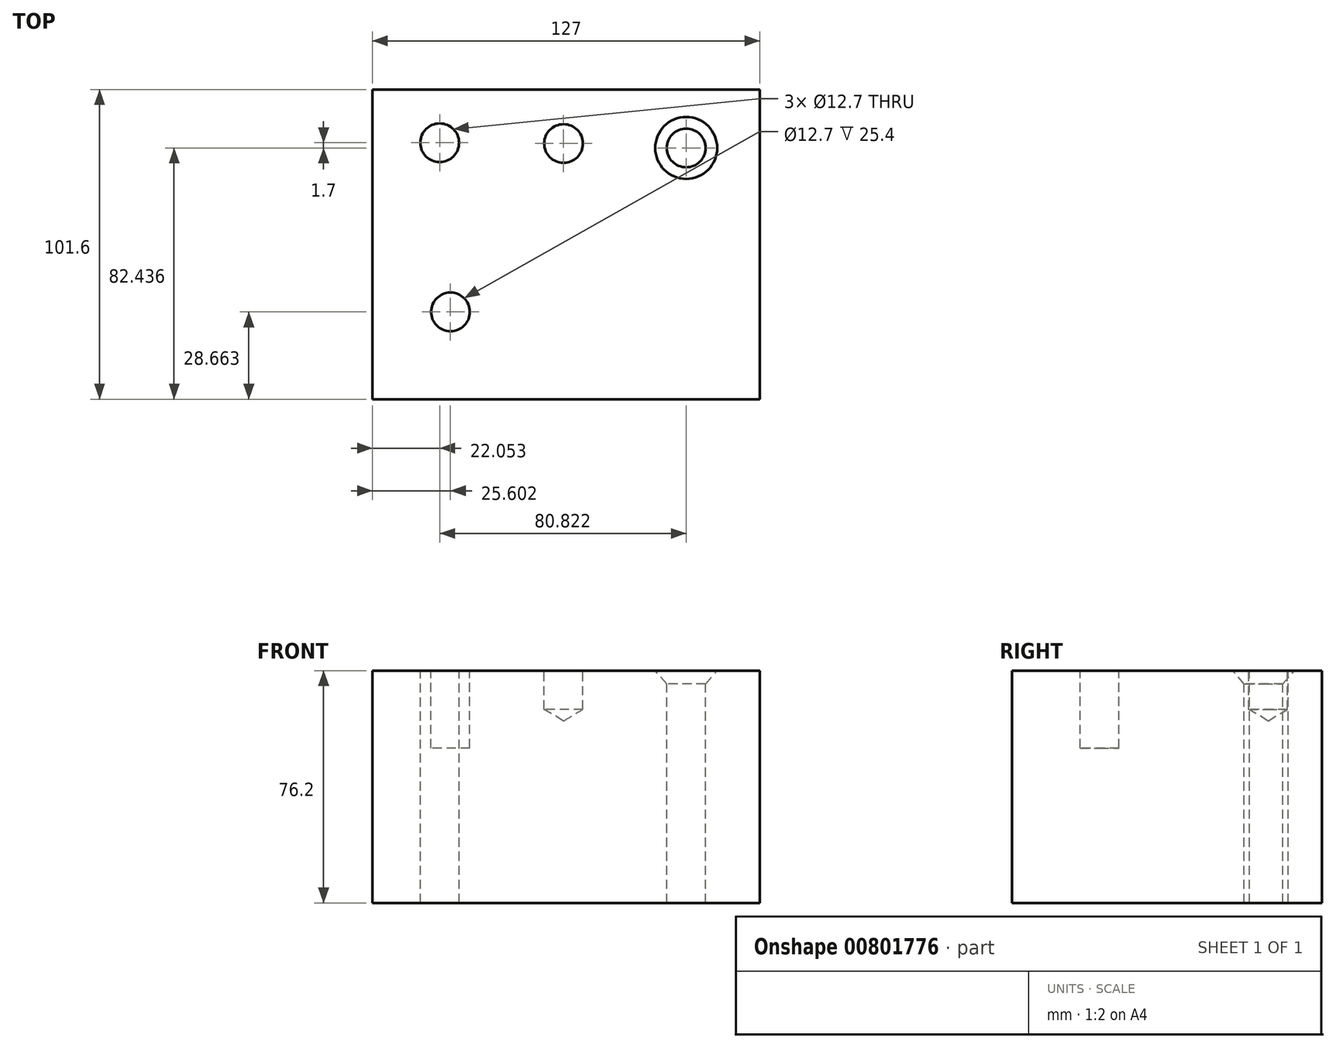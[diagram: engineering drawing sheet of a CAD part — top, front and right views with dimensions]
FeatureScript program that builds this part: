
annotation { "Feature Type Name" : "Feature", "Feature Type Description" : "" }
export const myFeature = defineFeature(function(context is Context, id is Id, definition is map)
    precondition{}
    {
        {
            var Q0;
            Q0=qCreatedBy(makeId("Top.planeOp"),FACE);
            var sketch = newSketch(context, id + "F0", { "sketchPlane" : qUnion([Q0])});
            skLineSegment(sketch, "E0.bottom", {"start": v(-55.05, 51.24) * mm, "end": v(71.95, 51.24) * mm});
            skLineSegment(sketch, "E0.top", {"start": v(-55.05, -50.36) * mm, "end": v(71.95, -50.36) * mm});
            skLineSegment(sketch, "E0.left", {"start": v(-55.05, 51.24) * mm, "end": v(-55.05, -50.36) * mm});
            skLineSegment(sketch, "E0.right", {"start": v(71.95, 51.24) * mm, "end": v(71.95, -50.36) * mm});
            skSolve(sketch);
        }
        {
            var Q0;
            Q0 = qSketchRegion(id + "F0", true);
            extrude(context, id + "F1", {"entities" : qUnion([Q0]), "depth" : 76.2 * mm, "offsetDistance" : 25.4 * mm});
        }
        {
            var Q0;
            Q0=makeQuery(id+"F1.opExtrude","CAP_FACE",FACE,{"disambiguationData":[OSD([sQuery(id+"F0.wireOp",EDGE,"E0.bottom"),sQuery(id+"F0.wireOp",EDGE,"E0.top"),sQuery(id+"F0.wireOp",EDGE,"E0.left"),sQuery(id+"F0.wireOp",EDGE,"E0.right")])],"isStart":false});
            var sketch = newSketch(context, id + "F2", { "sketchPlane" : qUnion([Q0])});
            skPoint(sketch, "E1", {"position": v(-33, 33.78) * mm});
            skPoint(sketch, "E2", {"position": v(7.63, 33.53) * mm});
            skPoint(sketch, "E3", {"position": v(47.83, 32.08) * mm});
            skPoint(sketch, "E4", {"position": v(-14.33, -25.97) * mm});
            skPoint(sketch, "E5", {"position": v(32.2, -27.84) * mm});
            skPoint(sketch, "E6", {"position": v(3.23, 2.39) * mm});
            skSolve(sketch);
        }
        {
            var Q0;
            Q0=sQuery(id+"F2.wireOp",VERTEX,"E1");
            var Q1;
            Q1=makeQuery(id+"F1.opExtrude","SWEPT_BODY",BODY,{"disambiguationData":[OSD([sQuery(id+"F0.wireOp",EDGE,"E0.bottom"),sQuery(id+"F0.wireOp",EDGE,"E0.top"),sQuery(id+"F0.wireOp",EDGE,"E0.left"),sQuery(id+"F0.wireOp",EDGE,"E0.right")])]});
            hole(context, id + "F3", {"style" : HoleStyle.SIMPLE, "endStyle" : HoleEndStyle.THROUGH, "holeDiameter" : 12.7 * mm, "majorDiameter" : 6.35 * mm, "isTappedThrough" : true, "tappedDepth" : 12.7 * mm, "tapClearance" : 3, "locations" : qUnion([Q0]), "scope" : qUnion([Q1])});
        }
        {
            var Q0;
            Q0=sQuery(id+"F2.wireOp",VERTEX,"E2");
            var Q1;
            Q1=makeQuery(id+"F1.opExtrude","SWEPT_BODY",BODY,{"disambiguationData":[OSD([sQuery(id+"F0.wireOp",EDGE,"E0.bottom"),sQuery(id+"F0.wireOp",EDGE,"E0.top"),sQuery(id+"F0.wireOp",EDGE,"E0.left"),sQuery(id+"F0.wireOp",EDGE,"E0.right")])]});
            hole(context, id + "F4", {"style" : HoleStyle.SIMPLE, "endStyle" : HoleEndStyle.BLIND, "holeDiameter" : 12.7 * mm, "majorDiameter" : 6.35 * mm, "holeDepth" : 12.7 * mm, "isTappedThrough" : true, "tappedDepth" : 12.7 * mm, "tapClearance" : 3, "locations" : qUnion([Q0]), "scope" : qUnion([Q1])});
        }
        {
            var Q0;
            Q0=sQuery(id+"F2.wireOp",VERTEX,"E3");
            var Q1;
            Q1=makeQuery(id+"F1.opExtrude","SWEPT_BODY",BODY,{"disambiguationData":[OSD([sQuery(id+"F0.wireOp",EDGE,"E0.bottom"),sQuery(id+"F0.wireOp",EDGE,"E0.top"),sQuery(id+"F0.wireOp",EDGE,"E0.left"),sQuery(id+"F0.wireOp",EDGE,"E0.right")])]});
            hole(context, id + "F5", {"style" : HoleStyle.C_SINK, "endStyle" : HoleEndStyle.THROUGH, "holeDiameter" : 12.7 * mm, "cSinkDiameter" : 20.32 * mm, "cSinkAngle" : 82 * degree, "majorDiameter" : 6.35 * mm, "isTappedThrough" : true, "tappedDepth" : 12.7 * mm, "tapClearance" : 3, "locations" : qUnion([Q0]), "scope" : qUnion([Q1])});
        }
        {
            var Q0;
            Q0=makeQuery(id+"F1.opExtrude","CAP_FACE",FACE,{"disambiguationData":[OSD([sQuery(id+"F0.wireOp",EDGE,"E0.bottom"),sQuery(id+"F0.wireOp",EDGE,"E0.top"),sQuery(id+"F0.wireOp",EDGE,"E0.left"),sQuery(id+"F0.wireOp",EDGE,"E0.right")])],"isStart":false});
            var sketch = newSketch(context, id + "F6", { "sketchPlane" : qUnion([Q0])});
            skCircle(sketch, "E7", {"center": v(-29.45, -21.7) * mm, "radius": 6.35 * mm});
            skSolve(sketch);
        }
        {
            var Q0;
            Q0 = qSketchRegion(id + "F6", true);
            extrude(context, id + "F7", {"entities" : qUnion([Q0]), "operationType" : NewBodyOperationType.REMOVE, "oppositeDirection" : true, "depth" : 25.4 * mm, "offsetDistance" : 25.4 * mm});
        }
    });
